# Revit family: M-1005
name_source: partatom
category: Plumbing Fixtures
revit_build: Autodesk Revit 2014 (Build: 20130308_1515(x64)
units: mm (PartAtom-declared; Revit-internal decimal feet)

## types (1)
- M-1005
    Accessories = Push Drain; Tool Clamping; Hidden Aerator; Key To Aerator; Insert Sink Without Overflow
    Brass Chromed = Brass
    Cartridge = Right V Valvex; Left V Valvex
    Data Sheet = http://helvex.com
    Description = Clásica Faucet With Push Drain
    Features = Sink Mixer With Drain Holes Push Apart; Installing 8" - 12"; With Valvex V Of Ceramic Discs Of ¼ To Turn
    Installation Thread = ½" - 14 NPSM
    Instructive = http://helvex.com
    Manufacturer = HELVEX
    Materials = Handle Brass; Body Brass; Push Drain Brass
    Max. Working Pressure = 85.3 psi
    Min. Working Pressure = 3.6 psi
    Model = M-1005
    Operation = The Handle Rotation Angle 90° To The Function Of Hot And Cold Water
    Total Depth = 8"
    Total Height = 7"
    Total Length = 18"
    Type Comments = Lavatory Faucet Assemblies
    URL = http://helvex.com

## geometry (parser evidence)
native form markers: Sweep x1
no freeform markers — native parametric forms only
